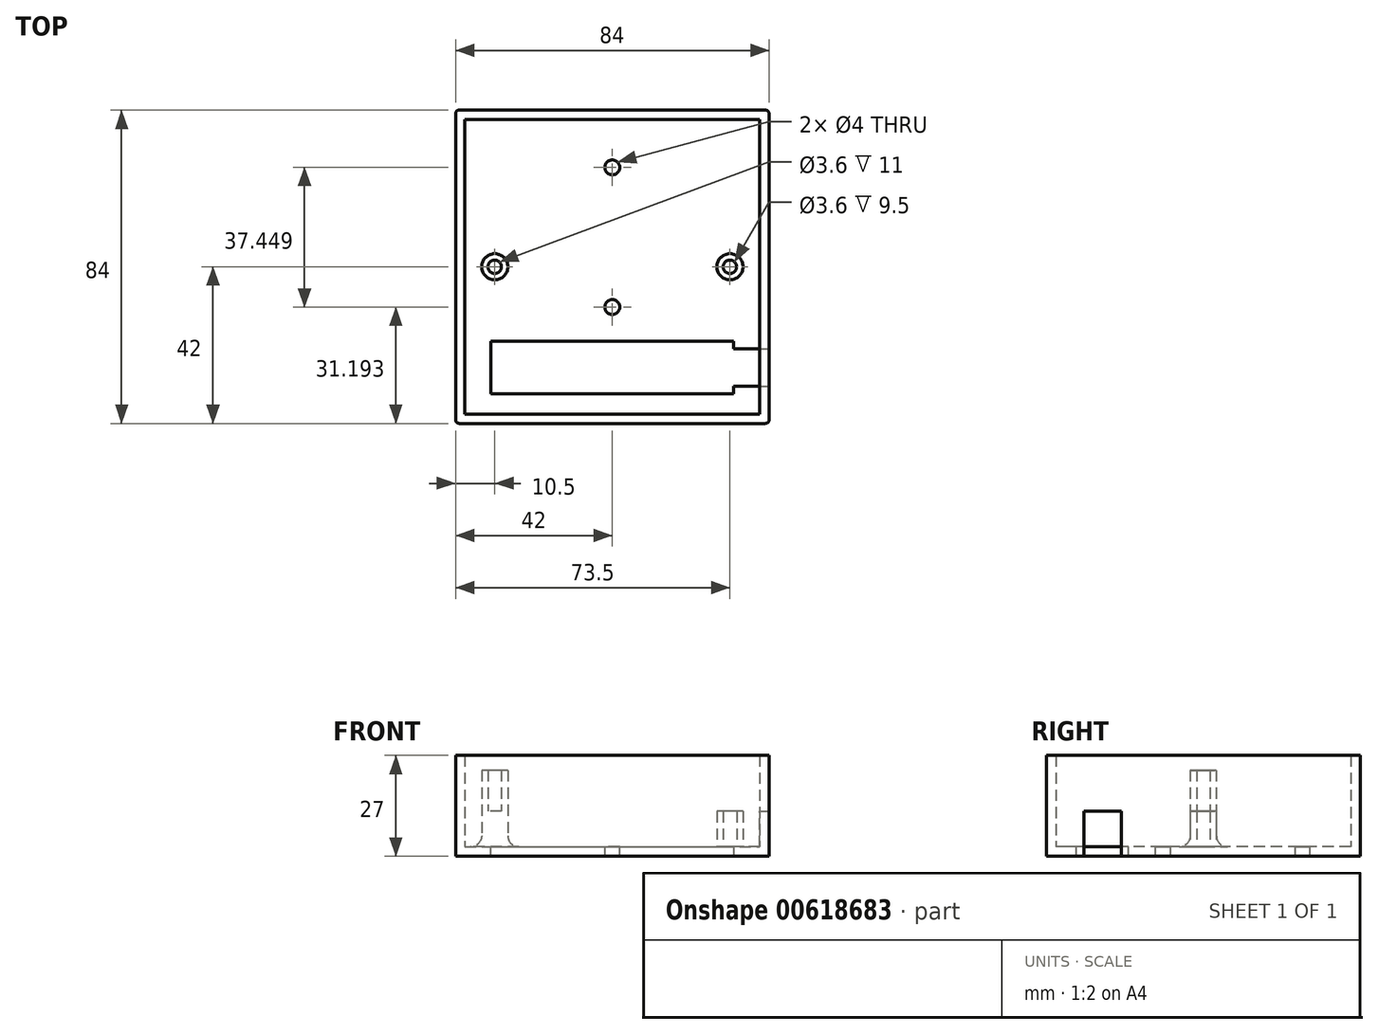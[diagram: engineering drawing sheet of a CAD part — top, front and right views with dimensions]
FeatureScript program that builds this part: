
annotation { "Feature Type Name" : "Feature", "Feature Type Description" : "" }
export const myFeature = defineFeature(function(context is Context, id is Id, definition is map)
    precondition{}
    {
        {
            var Q0;
            Q0=qCreatedBy(makeId("Top.planeOp"),FACE);
            var sketch = newSketch(context, id + "F0", { "sketchPlane" : qUnion([Q0])});
            skLineSegment(sketch, "E0.bottom", {"start": v(-42, 42) * mm, "end": v(42, 42) * mm});
            skLineSegment(sketch, "E0.top", {"start": v(-42, -42) * mm, "end": v(42, -42) * mm});
            skLineSegment(sketch, "E0.left", {"start": v(-42, 42) * mm, "end": v(-42, -42) * mm});
            skLineSegment(sketch, "E0.right", {"start": v(42, 42) * mm, "end": v(42, -42) * mm});
            skPoint(sketch, "E0.middle", {"position": v(0, 0) * mm});
            skSolve(sketch);
        }
        {
            var Q0;
            Q0=makeQuery(id+"F0.imprint","IMPRINT",FACE,{"disambiguationData":[TD([[makeQuery(id+"F0.imprint","IMPRINT",EDGE,{"derivedFrom":sQuery(id+"F0.wireOp",EDGE,"E0.bottom")}),-1.0]])]});
            extrude(context, id + "F1", {"entities" : qUnion([Q0]), "depth" : 27 * mm, "offsetDistance" : 25 * mm});
        }
        {
            var Q0;
            Q0=makeQuery(id+"F1.opExtrude","CAP_FACE",FACE,{"disambiguationData":[OSD([sQuery(id+"F0.wireOp",EDGE,"E0.bottom"),sQuery(id+"F0.wireOp",EDGE,"E0.top"),sQuery(id+"F0.wireOp",EDGE,"E0.left"),sQuery(id+"F0.wireOp",EDGE,"E0.right")])],"isStart":false});
            shell(context, id + "F2", {"entities" : qUnion([Q0]), "thickness" : 2.5 * mm});
        }
        {
            var Q0;
            Q0=makeQuery(id+"F2.opShell","OFFSET_FACE",FACE,{"disambiguationData":[OSD([sQuery(id+"F0.wireOp",EDGE,"E0.bottom"),sQuery(id+"F0.wireOp",EDGE,"E0.top"),sQuery(id+"F0.wireOp",EDGE,"E0.left"),sQuery(id+"F0.wireOp",EDGE,"E0.right")])]});
            extrude(context, id + "F3", {"entities" : qUnion([Q0]), "operationType" : NewBodyOperationType.REMOVE, "depth" : 2 * mm, "offsetDistance" : 25 * mm});
        }
        {
            var Q0;
            {var subQ0=sQuery(id+"F0.wireOp",EDGE,"dfe78086-a53e-4b4b-9db1-65955daeefa80.MirrorC");var subQ1=sQuery(id+"F0.wireOp",EDGE,"WS2b7sYa-ZVix-v7k1-hiQI-JHHMlIN35ILA");var subQ2=sQuery(id+"F0.wireOp",EDGE,"E0.right");var subQ3=sQuery(id+"F0.wireOp",EDGE,"E0.left");var subQ4=sQuery(id+"F0.wireOp",EDGE,"E0.top");var subQ5=sQuery(id+"F0.wireOp",EDGE,"E0.bottom");Q0=makeQuery(id+"F2.opShell","OFFSET_FACE",FACE,{"disambiguationData":[OSD([subQ5,subQ4,subQ3,subQ2,subQ1,subQ0]),TDD([makeQuery(id+"F1.opExtrude","CAP_FACE",FACE,{"disambiguationData":[OSD([subQ5,subQ4,subQ3,subQ2,subQ1,subQ0])],"isStart":true})])]});}
            var sketch = newSketch(context, id + "F4", { "sketchPlane" : qUnion([Q0])});
            skLineSegment(sketch, "E1.bottom", {"start": v(-32.5, -20) * mm, "end": v(32.5, -20) * mm});
            skLineSegment(sketch, "E1.top", {"start": v(-32.5, -34) * mm, "end": v(32.5, -34) * mm});
            skLineSegment(sketch, "E1.left", {"start": v(-32.5, -20) * mm, "end": v(-32.5, -34) * mm});
            skLineSegment(sketch, "E1.right", {"start": v(32.5, -20) * mm, "end": v(32.5, -34) * mm});
            skPoint(sketch, "E1.middle", {"position": v(0, -27) * mm});
            skCircle(sketch, "E2", {"center": v(0, 26.64) * mm, "radius": 2 * mm});
            skCircle(sketch, "E3", {"center": v(0, -10.8) * mm, "radius": 2 * mm});
            skSolve(sketch);
        }
        {
            var Q0;
            Q0=makeQuery(id+"F4.imprint","IMPRINT",FACE,{"disambiguationData":[TD([[makeQuery(id+"F4.imprint","IMPRINT",EDGE,{"derivedFrom":sQuery(id+"F4.wireOp",EDGE,"I27aAWvG-3vU7-xFHq-uyNN-OG2R7n4DVnkj")}),1.0]])]});
            var Q1;
            Q1=makeQuery(id+"F4.imprint","IMPRINT",FACE,{"disambiguationData":[TD([[makeQuery(id+"F4.imprint","IMPRINT",EDGE,{"derivedFrom":sQuery(id+"F4.wireOp",EDGE,"E1.bottom")}),-1.0]])]});
            extrude(context, id + "F5", {"entities" : qUnion([Q0, Q1]), "operationType" : NewBodyOperationType.REMOVE, "oppositeDirection" : true, "depth" : 25 * mm, "offsetDistance" : 25 * mm});
        }
        {
            var Q0;
            Q0=makeQuery(id+"F1.opExtrude","SWEPT_FACE",FACE,{"disambiguationData":[OSD([sQuery(id+"F0.wireOp",EDGE,"E0.right")])]});
            var sketch = newSketch(context, id + "F6", { "sketchPlane" : qUnion([Q0])});
            skLineSegment(sketch, "E4.bottom", {"start": v(-22, 0) * mm, "end": v(-32, 0) * mm});
            skLineSegment(sketch, "E4.top", {"start": v(-22, 10) * mm, "end": v(-32, 10) * mm});
            skLineSegment(sketch, "E4.left", {"start": v(-22, 0) * mm, "end": v(-22, 10) * mm});
            skLineSegment(sketch, "E4.right", {"start": v(-32, 0) * mm, "end": v(-32, 10) * mm});
            skPoint(sketch, "E4.middle", {"position": v(-27, 5) * mm});
            skSolve(sketch);
        }
        {
            var Q0;
            Q0=makeQuery(id+"F6.imprint","IMPRINT",FACE,{"disambiguationData":[TD([[makeQuery(id+"F6.imprint","IMPRINT",EDGE,{"derivedFrom":sQuery(id+"F6.wireOp",EDGE,"E4.bottom")}),-1.0]])]});
            extrude(context, id + "F7", {"entities" : qUnion([Q0]), "operationType" : NewBodyOperationType.REMOVE, "oppositeDirection" : true, "depth" : 21.8 * mm, "offsetDistance" : 25 * mm});
        }
        {
            var Q0;
            Q0=makeQuery(id+"F4.imprint","IMPRINT",FACE,{"disambiguationData":[TD([[makeQuery(id+"F4.imprint","IMPRINT",EDGE,{"derivedFrom":sQuery(id+"F4.wireOp",EDGE,"E2")}),1.0]])]});
            var Q1;
            Q1=makeQuery(id+"F4.imprint","IMPRINT",FACE,{"disambiguationData":[TD([[makeQuery(id+"F4.imprint","IMPRINT",EDGE,{"derivedFrom":sQuery(id+"F4.wireOp",EDGE,"E3")}),1.0]])]});
            extrude(context, id + "F8", {"entities" : qUnion([Q0, Q1]), "operationType" : NewBodyOperationType.REMOVE, "oppositeDirection" : true, "depth" : 25 * mm, "offsetDistance" : 25 * mm});
        }
        {
            var Q0;
            Q0=makeQuery(id+"F1.opExtrude","CAP_FACE",FACE,{"disambiguationData":[OSD([sQuery(id+"F0.wireOp",EDGE,"E0.bottom"),sQuery(id+"F0.wireOp",EDGE,"E0.top"),sQuery(id+"F0.wireOp",EDGE,"E0.left"),sQuery(id+"F0.wireOp",EDGE,"E0.right"),sQuery(id+"F0.wireOp",EDGE,"WS2b7sYa-ZVix-v7k1-hiQI-JHHMlIN35ILA"),sQuery(id+"F0.wireOp",EDGE,"dfe78086-a53e-4b4b-9db1-65955daeefa80.MirrorC")])],"isStart":false});
            var Q1;
            {var subQ0=sQuery(id+"F0.wireOp",EDGE,"dfe78086-a53e-4b4b-9db1-65955daeefa80.MirrorC");var subQ1=sQuery(id+"F0.wireOp",EDGE,"WS2b7sYa-ZVix-v7k1-hiQI-JHHMlIN35ILA");var subQ2=sQuery(id+"F0.wireOp",EDGE,"E0.right");var subQ3=sQuery(id+"F0.wireOp",EDGE,"E0.left");var subQ4=sQuery(id+"F0.wireOp",EDGE,"E0.top");var subQ5=sQuery(id+"F0.wireOp",EDGE,"E0.bottom");Q1=makeQuery(id+"F2.opShell","OFFSET_FACE",FACE,{"disambiguationData":[OSD([subQ5,subQ4,subQ3,subQ2,subQ1,subQ0]),TDD([makeQuery(id+"F1.opExtrude","CAP_FACE",FACE,{"disambiguationData":[OSD([subQ5,subQ4,subQ3,subQ2,subQ1,subQ0])],"isStart":false})]),OD(1.0)]});}
            extrude(context, id + "F9", {"entities" : qUnion([Q0, Q1]), "operationType" : NewBodyOperationType.REMOVE, "oppositeDirection" : true, "depth" : 2 * mm, "offsetDistance" : 25 * mm});
        }
        {
            var Q0;
            Q0=qCreatedBy(makeId("Top.planeOp"),FACE);
            var sketch = newSketch(context, id + "F10", { "sketchPlane" : qUnion([Q0])});
            skCircle(sketch, "E5", {"center": v(-31.5, 0) * mm, "radius": 3.5 * mm});
            skCircle(sketch, "E6.MirrorC", {"center": v(31.5, 0) * mm, "radius": 3.5 * mm});
            skCircle(sketch, "E7", {"center": v(-31.5, 0) * mm, "radius": 1.8 * mm});
            skCircle(sketch, "E8.MirrorC", {"center": v(31.5, 0) * mm, "radius": 1.8 * mm});
            skSolve(sketch);
        }
        {
            var Q0;
            Q0=makeQuery(id+"F10.imprint","IMPRINT",FACE,{"disambiguationData":[TD([[makeQuery(id+"F10.imprint","IMPRINT",EDGE,{"derivedFrom":sQuery(id+"F10.wireOp",EDGE,"E5")}),1.0]])]});
            var Q1;
            Q1=makeQuery(id+"F10.imprint","IMPRINT",FACE,{"disambiguationData":[TD([[makeQuery(id+"F10.imprint","IMPRINT",EDGE,{"derivedFrom":sQuery(id+"F10.wireOp",EDGE,"E6.MirrorC")}),-1.0]])]});
            extrude(context, id + "F11", {"entities" : qUnion([Q0, Q1]), "operationType" : NewBodyOperationType.ADD, "depth" : 21 * mm, "offsetDistance" : 25 * mm});
        }
        {
            var Q0;
            Q0=makeQuery(id+"F10.imprint","IMPRINT",FACE,{"disambiguationData":[TD([[makeQuery(id+"F10.imprint","IMPRINT",EDGE,{"derivedFrom":sQuery(id+"F10.wireOp",EDGE,"E7")}),1.0]])]});
            var Q1;
            Q1=makeQuery(id+"F10.imprint","IMPRINT",FACE,{"disambiguationData":[TD([[makeQuery(id+"F10.imprint","IMPRINT",EDGE,{"derivedFrom":sQuery(id+"F10.wireOp",EDGE,"E8.MirrorC")}),-1.0]])]});
            extrude(context, id + "F12", {"entities" : qUnion([Q0, Q1]), "operationType" : NewBodyOperationType.ADD, "depth" : 10 * mm, "offsetDistance" : 25 * mm});
        }
        {
            var Q0;
            Q0=makeQuery(id+"F1.opExtrude","SWEPT_EDGE",EDGE,{"disambiguationData":[OSD([sQuery(id+"F0.wireOp",EDGE,"E0.bottom"),sQuery(id+"F0.wireOp",EDGE,"E0.left")])]});
            var Q1;
            Q1=makeQuery(id+"F1.opExtrude","SWEPT_EDGE",EDGE,{"disambiguationData":[OSD([sQuery(id+"F0.wireOp",EDGE,"E0.bottom"),sQuery(id+"F0.wireOp",EDGE,"E0.right")])]});
            var Q2;
            Q2=makeQuery(id+"F1.opExtrude","SWEPT_EDGE",EDGE,{"disambiguationData":[OSD([sQuery(id+"F0.wireOp",EDGE,"E0.top"),sQuery(id+"F0.wireOp",EDGE,"E0.right")])]});
            var Q3;
            Q3=makeQuery(id+"F1.opExtrude","SWEPT_EDGE",EDGE,{"disambiguationData":[OSD([sQuery(id+"F0.wireOp",EDGE,"E0.top"),sQuery(id+"F0.wireOp",EDGE,"E0.left")])]});
            fillet(context, id + "F13", {"entities" : qUnion([Q0, Q1, Q2, Q3]), "radius" : 1 * mm, "tangentPropagation" : true, "allowEdgeOverflow" : false});
        }
        {
            var Q0;
            Q0=makeQuery(id+"F1.opExtrude","CAP_FACE",FACE,{"disambiguationData":[OSD([sQuery(id+"F0.wireOp",EDGE,"E0.bottom"),sQuery(id+"F0.wireOp",EDGE,"E0.top"),sQuery(id+"F0.wireOp",EDGE,"E0.left"),sQuery(id+"F0.wireOp",EDGE,"E0.right")])],"isStart":true});
            extrude(context, id + "F14", {"entities" : qUnion([Q0]), "operationType" : NewBodyOperationType.ADD, "depth" : 2 * mm, "offsetDistance" : 25 * mm});
        }
        {
            var Q0;
            {var subQ0=sQuery(id+"F0.wireOp",EDGE,"E0.right");var subQ1=sQuery(id+"F0.wireOp",EDGE,"E0.left");var subQ2=sQuery(id+"F0.wireOp",EDGE,"E0.top");var subQ3=sQuery(id+"F0.wireOp",EDGE,"E0.bottom");Q0=makeQuery(id+"F11.boolean.opBoolean","INTERSECT",EDGE,{"derivedFrom":[makeQuery(id+"F9.boolean.opBoolean","COPY",FACE,{"derivedFrom":makeQuery(id+"F9.opExtrude","CAP_FACE",FACE,{"disambiguationData":[OSD([subQ3,subQ2,subQ1,subQ0]),TDD([makeQuery(id+"F2.opShell","OFFSET_FACE",FACE,{"disambiguationData":[OSD([subQ3,subQ2,subQ1,subQ0])]})])],"isStart":false})}),makeQuery(id+"F11.opExtrude","SWEPT_FACE",FACE,{"disambiguationData":[OSD([sQuery(id+"F10.wireOp",EDGE,"E5")])]})]});}
            var Q1;
            {var subQ0=sQuery(id+"F0.wireOp",EDGE,"E0.right");var subQ1=sQuery(id+"F0.wireOp",EDGE,"E0.left");var subQ2=sQuery(id+"F0.wireOp",EDGE,"E0.top");var subQ3=sQuery(id+"F0.wireOp",EDGE,"E0.bottom");Q1=makeQuery(id+"F11.boolean.opBoolean","INTERSECT",EDGE,{"derivedFrom":[makeQuery(id+"F9.boolean.opBoolean","COPY",FACE,{"derivedFrom":makeQuery(id+"F9.opExtrude","CAP_FACE",FACE,{"disambiguationData":[OSD([subQ3,subQ2,subQ1,subQ0]),TDD([makeQuery(id+"F2.opShell","OFFSET_FACE",FACE,{"disambiguationData":[OSD([subQ3,subQ2,subQ1,subQ0])]})])],"isStart":false})}),makeQuery(id+"F11.opExtrude","SWEPT_FACE",FACE,{"disambiguationData":[OSD([sQuery(id+"F10.wireOp",EDGE,"E6.MirrorC")])]})]});}
            fillet(context, id + "F15", {"entities" : qUnion([Q0, Q1]), "radius" : 3 * mm, "tangentPropagation" : true, "allowEdgeOverflow" : false});
        }
    });
